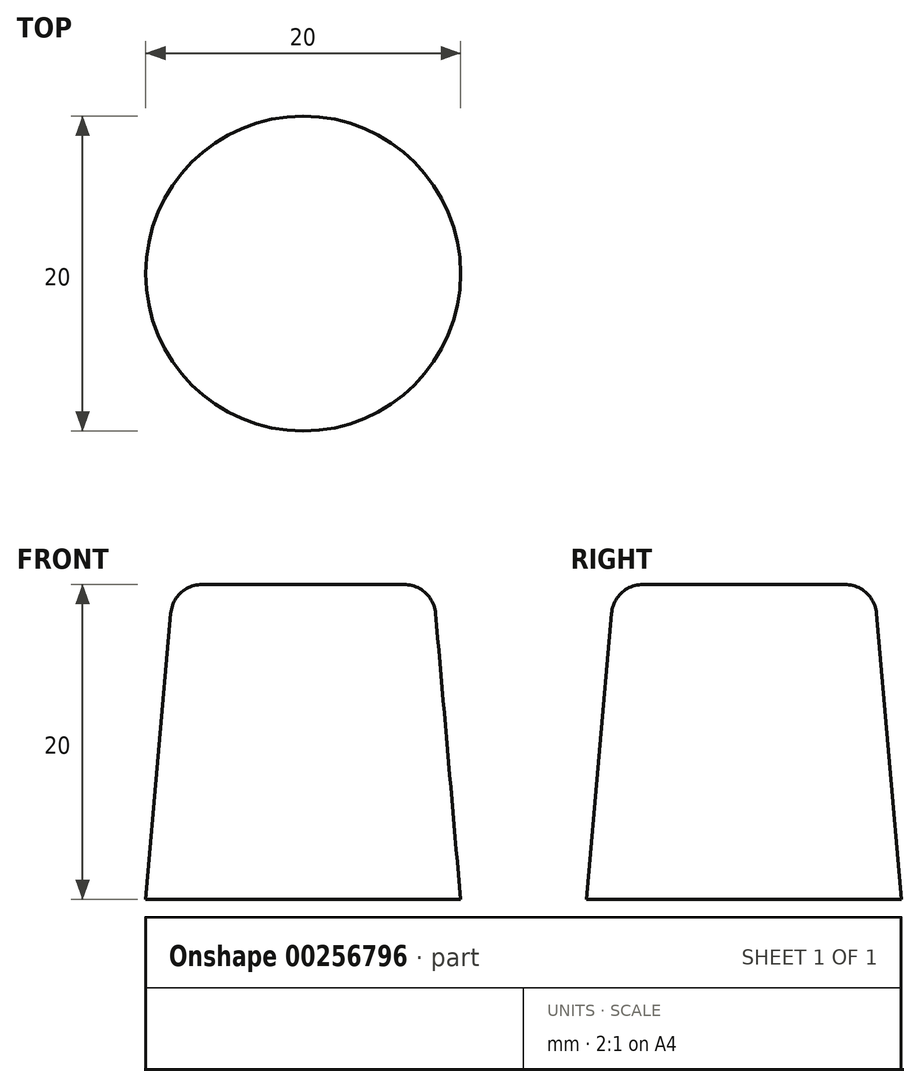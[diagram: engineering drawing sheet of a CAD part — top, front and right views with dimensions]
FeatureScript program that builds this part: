
annotation { "Feature Type Name" : "Feature", "Feature Type Description" : "" }
export const myFeature = defineFeature(function(context is Context, id is Id, definition is map)
    precondition{}
    {
        {
            var Q0;
            Q0=qCreatedBy(makeId("Top.planeOp"),FACE);
            var sketch = newSketch(context, id + "F0", { "sketchPlane" : qUnion([Q0])});
            skCircle(sketch, "E0", {"center": v(0, 0) * mm, "radius": 10 * mm});
            skSolve(sketch);
        }
        {
            var Q0;
            Q0=qSketchRegion(id+"F0",true);
            extrude(context, id + "F1", {"entities" : qUnion([Q0]), "depth" : 20 * mm, "hasDraft" : true, "draftAngle" : 5 * degree, "draftPullDirection" : true});
        }
        {
            var Q0;
            Q0=makeQuery(id+"F1.opExtrude","CAP_EDGE",EDGE,{"disambiguationData":[OSD([sQuery(id+"F0.wireOp",EDGE,"E0")])],"isStart":false});
            fillet(context, id + "F2", {"entities" : qUnion([Q0]), "radius" : 2 * mm, "tangentPropagation" : true, "allowEdgeOverflow" : false});
        }
    });
